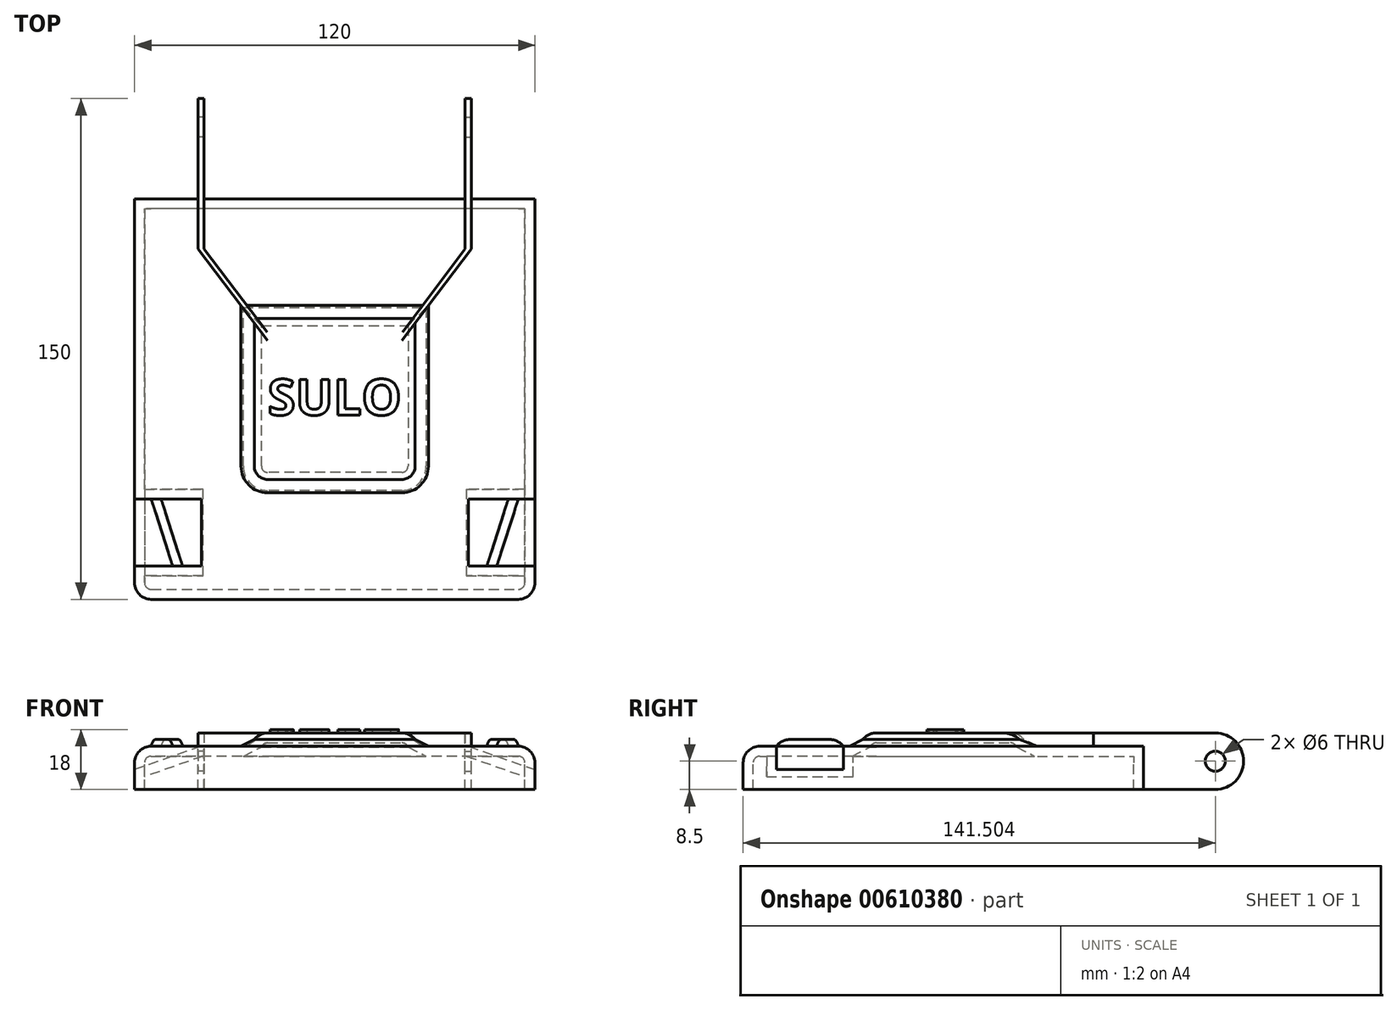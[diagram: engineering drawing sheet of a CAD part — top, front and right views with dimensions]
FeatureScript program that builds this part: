
annotation { "Feature Type Name" : "Feature", "Feature Type Description" : "" }
export const myFeature = defineFeature(function(context is Context, id is Id, definition is map)
    precondition{}
    {
        {
            var Q0;
            Q0=qCreatedBy(makeId("Top.planeOp"),FACE);
            var sketch = newSketch(context, id + "F0", { "sketchPlane" : qUnion([Q0])});
            skLineSegment(sketch, "E0.bottom", {"start": v(-158.38, 187.53) * mm, "end": v(-38.38, 187.53) * mm});
            skLineSegment(sketch, "E0.top", {"start": v(-158.38, 37.53) * mm, "end": v(-38.38, 37.53) * mm});
            skLineSegment(sketch, "E0.left", {"start": v(-158.38, 187.53) * mm, "end": v(-158.38, 37.53) * mm});
            skLineSegment(sketch, "E0.right", {"start": v(-38.38, 187.53) * mm, "end": v(-38.38, 37.53) * mm});
            skSolve(sketch);
        }
        {
            var Q0;
            Q0=makeQuery(id+"F0.imprint","IMPRINT",FACE,{"disambiguationData":[TD([[makeQuery(id+"F0.imprint","IMPRINT",EDGE,{"derivedFrom":sQuery(id+"F0.wireOp",EDGE,"E0.bottom")}),-1.0]])]});
            extrude(context, id + "F1", {"entities" : qUnion([Q0]), "depth" : 13 * mm, "offsetDistance" : 25 * mm});
        }
        {
            var Q0;
            Q0=makeQuery(id+"F1.opExtrude","CAP_FACE",FACE,{"disambiguationData":[OSD([sQuery(id+"F0.wireOp",EDGE,"E0.bottom"),sQuery(id+"F0.wireOp",EDGE,"E0.top"),sQuery(id+"F0.wireOp",EDGE,"E0.left"),sQuery(id+"F0.wireOp",EDGE,"E0.right")])],"isStart":false});
            var sketch = newSketch(context, id + "F2", { "sketchPlane" : qUnion([Q0])});
            skLineSegment(sketch, "E1", {"start": v(-73.38, 72.53) * mm, "end": v(-123.38, 72.53) * mm});
            skLineSegment(sketch, "E2", {"start": v(-123.38, 72.53) * mm, "end": v(-123.38, 121.53) * mm});
            skLineSegment(sketch, "E3", {"start": v(-122.38, 122.53) * mm, "end": v(-74.38, 122.53) * mm});
            skLineSegment(sketch, "E4", {"start": v(-73.38, 121.53) * mm, "end": v(-73.38, 72.53) * mm});
            skLineSegment(sketch, "E5", {"start": v(-139.38, 187.53) * mm, "end": v(-139.38, 142.53) * mm});
            skLineSegment(sketch, "E6", {"start": v(-139.38, 142.53) * mm, "end": v(-123.38, 121.53) * mm});
            skLineSegment(sketch, "E7", {"start": v(-122.38, 122.53) * mm, "end": v(-137.63, 142.53) * mm});
            skLineSegment(sketch, "E8", {"start": v(-137.63, 142.53) * mm, "end": v(-137.63, 187.53) * mm});
            skLineSegment(sketch, "E9", {"start": v(-57.38, 187.53) * mm, "end": v(-57.38, 142.53) * mm});
            skLineSegment(sketch, "E10", {"start": v(-57.38, 142.53) * mm, "end": v(-73.38, 121.53) * mm});
            skLineSegment(sketch, "E11", {"start": v(-59.38, 187.53) * mm, "end": v(-59.38, 142.53) * mm});
            skLineSegment(sketch, "E12", {"start": v(-59.38, 142.53) * mm, "end": v(-74.38, 122.53) * mm});
            skSolve(sketch);
        }
        {
            var Q0;
            Q0=makeQuery(id+"F2.imprint","IMPRINT",FACE,{"disambiguationData":[TD([[makeQuery(id+"F2.imprint","IMPRINT",EDGE,{"derivedFrom":sQuery(id+"F2.wireOp",EDGE,"E1")}),-1.0]])]});
            extrude(context, id + "F3", {"entities" : qUnion([Q0]), "operationType" : NewBodyOperationType.ADD, "depth" : 4 * mm, "offsetDistance" : 25 * mm});
        }
        {
            var Q0;
            {var subQ1=sQuery(id+"F0.wireOp",EDGE,"E0.left");var subQ3=sQuery(id+"F0.wireOp",EDGE,"E0.bottom");var subQ4=sQuery(id+"F0.wireOp",EDGE,"E0.right");var subQ5=sQuery(id+"F0.wireOp",EDGE,"E0.top");Q0=makeQuery(id+"F3.boolean.opBoolean","SPLIT",FACE,{"disambiguationData":[TD([makeQuery(id+"F1.opExtrude","SWEPT_FACE",FACE,{"disambiguationData":[OSD([subQ5])]})])],"derivedFrom":makeQuery(id+"F1.opExtrude","CAP_FACE",FACE,{"disambiguationData":[OSD([subQ3,subQ5,subQ1,subQ4])],"isStart":false})});}
            var sketch = newSketch(context, id + "F4", { "sketchPlane" : qUnion([Q0])});
            skLineSegment(sketch, "E13", {"start": v(-38.38, 187.53) * mm, "end": v(-38.38, 157.53) * mm});
            skLineSegment(sketch, "E14", {"start": v(-38.38, 157.53) * mm, "end": v(-57.38, 157.53) * mm});
            skLineSegment(sketch, "E15", {"start": v(-57.38, 157.53) * mm, "end": v(-57.38, 187.53) * mm});
            skLineSegment(sketch, "E16", {"start": v(-57.38, 187.53) * mm, "end": v(-38.38, 187.53) * mm});
            skLineSegment(sketch, "E17", {"start": v(-139.38, 187.53) * mm, "end": v(-139.38, 157.53) * mm});
            skLineSegment(sketch, "E18", {"start": v(-139.38, 157.53) * mm, "end": v(-158.38, 157.53) * mm});
            skLineSegment(sketch, "E19", {"start": v(-158.38, 157.53) * mm, "end": v(-158.38, 187.53) * mm});
            skLineSegment(sketch, "E20", {"start": v(-158.38, 187.53) * mm, "end": v(-139.38, 187.53) * mm});
            skSolve(sketch);
        }
        {
            var Q0;
            Q0 = qSketchRegion(id + "F4", true);
            extrude(context, id + "F5", {"entities" : qUnion([Q0]), "operationType" : NewBodyOperationType.REMOVE, "oppositeDirection" : true, "depth" : 25 * mm, "offsetDistance" : 25 * mm});
        }
        {
            var Q0;
            {var subQ1=sQuery(id+"F0.wireOp",EDGE,"E0.bottom");Q0=makeQuery(id+"F3.boolean.opBoolean","SPLIT",FACE,{"disambiguationData":[TD([makeQuery(id+"F3.opExtrude","SWEPT_FACE",FACE,{"disambiguationData":[OSD([sQuery(id+"F2.wireOp",EDGE,"E3")])]})])],"derivedFrom":makeQuery(id+"F1.opExtrude","CAP_FACE",FACE,{"disambiguationData":[OSD([subQ1,sQuery(id+"F0.wireOp",EDGE,"E0.top"),sQuery(id+"F0.wireOp",EDGE,"E0.left"),sQuery(id+"F0.wireOp",EDGE,"E0.right")])],"isStart":false})});}
            var sketch = newSketch(context, id + "F6", { "sketchPlane" : qUnion([Q0])});
            skLineSegment(sketch, "E21", {"start": v(-137.63, 187.53) * mm, "end": v(-59.38, 187.53) * mm});
            skLineSegment(sketch, "E22", {"start": v(-59.38, 187.53) * mm, "end": v(-59.38, 157.53) * mm});
            skLineSegment(sketch, "E23", {"start": v(-59.38, 157.53) * mm, "end": v(-137.63, 157.53) * mm});
            skLineSegment(sketch, "E24", {"start": v(-137.63, 157.53) * mm, "end": v(-137.63, 187.53) * mm});
            skSolve(sketch);
        }
        {
            var Q0;
            Q0 = qSketchRegion(id + "F6", true);
            extrude(context, id + "F7", {"entities" : qUnion([Q0]), "operationType" : NewBodyOperationType.REMOVE, "oppositeDirection" : true, "depth" : 25 * mm, "offsetDistance" : 25 * mm});
        }
        {
            var Q0;
            {var subQ0=sQuery(id+"F0.wireOp",EDGE,"E0.bottom");var subQ1=makeQuery(id+"F1.opExtrude","CAP_EDGE",EDGE,{"disambiguationData":[OSD([subQ0])],"isStart":false});Q0=makeQuery(id+"F3.opExtrude","CAP_EDGE",EDGE,{"disambiguationData":[OSD([subQ0]),TDD([makeQuery(id+"F2.imprint","IMPRINT",EDGE,{"disambiguationData":[TD([[makeQuery(id+"F2.imprint","INTERSECT",VERTEX,{"derivedFrom":[subQ1,sQuery(id+"F2.wireOp",EDGE,"E9")]}),1.0]])],"derivedFrom":subQ1})])],"isStart":false});}
            var Q1;
            {var subQ0=sQuery(id+"F2.wireOp",EDGE,"E9");var subQ1=sQuery(id+"F0.wireOp",EDGE,"E0.bottom");Q1=makeQuery(id+"F7.boolean.opBoolean","SPLIT",EDGE,{"disambiguationData":[TD([makeQuery(id+"F3.opExtrude","SWEPT_FACE",FACE,{"disambiguationData":[OSD([subQ0])]})])],"derivedFrom":makeQuery(id+"F1.opExtrude","CAP_EDGE",EDGE,{"disambiguationData":[OSD([subQ1])],"isStart":true})});}
            var Q2;
            {var subQ0=sQuery(id+"F0.wireOp",EDGE,"E0.bottom");var subQ1=makeQuery(id+"F1.opExtrude","CAP_EDGE",EDGE,{"disambiguationData":[OSD([subQ0])],"isStart":false});Q2=makeQuery(id+"F3.opExtrude","CAP_EDGE",EDGE,{"disambiguationData":[OSD([subQ0]),TDD([makeQuery(id+"F2.imprint","IMPRINT",EDGE,{"disambiguationData":[TD([[makeQuery(id+"F2.imprint","INTERSECT",VERTEX,{"derivedFrom":[subQ1,sQuery(id+"F2.wireOp",EDGE,"E5")]}),-1.0]])],"derivedFrom":subQ1})])],"isStart":false});}
            var Q3;
            {var subQ1=sQuery(id+"F2.wireOp",EDGE,"E5");var subQ2=sQuery(id+"F0.wireOp",EDGE,"E0.bottom");Q3=makeQuery(id+"F7.boolean.opBoolean","SPLIT",EDGE,{"disambiguationData":[TD([makeQuery(id+"F3.opExtrude","SWEPT_FACE",FACE,{"disambiguationData":[OSD([subQ1])]})])],"derivedFrom":makeQuery(id+"F1.opExtrude","CAP_EDGE",EDGE,{"disambiguationData":[OSD([subQ2])],"isStart":true})});}
            fillet(context, id + "F8", {"entities" : qUnion([Q0, Q1, Q2, Q3]), "radius" : 8.5 * mm, "tangentPropagation" : true, "allowEdgeOverflow" : false});
        }
        {
            var Q0;
            Q0=makeQuery(id+"F3.opExtrude","CAP_EDGE",EDGE,{"disambiguationData":[OSD([sQuery(id+"F2.wireOp",EDGE,"E4")])],"isStart":false});
            var Q1;
            Q1=makeQuery(id+"F3.opExtrude","CAP_EDGE",EDGE,{"disambiguationData":[OSD([sQuery(id+"F2.wireOp",EDGE,"E3")])],"isStart":false});
            var Q2;
            Q2=makeQuery(id+"F3.opExtrude","CAP_EDGE",EDGE,{"disambiguationData":[OSD([sQuery(id+"F2.wireOp",EDGE,"E1")])],"isStart":false});
            var Q3;
            Q3=makeQuery(id+"F3.opExtrude","CAP_EDGE",EDGE,{"disambiguationData":[OSD([sQuery(id+"F2.wireOp",EDGE,"E2")])],"isStart":false});
            fillet(context, id + "F9", {"entities" : qUnion([Q0, Q1, Q2, Q3]), "radius" : 5 * mm, "tangentPropagation" : true, "allowEdgeOverflow" : false});
        }
        {
            var Q0;
            Q0=makeQuery(id+"F9.opFillet","BLEND_EDGE",EDGE,{"blendedFrom":[makeQuery(id+"F3.opExtrude","CAP_EDGE",EDGE,{"disambiguationData":[OSD([sQuery(id+"F2.wireOp",EDGE,"E1")])],"isStart":false}),makeQuery(id+"F3.opExtrude","CAP_EDGE",EDGE,{"disambiguationData":[OSD([sQuery(id+"F2.wireOp",EDGE,"E2")])],"isStart":false})],"blendedInto":[]});
            var Q1;
            Q1=makeQuery(id+"F9.opFillet","BLEND_EDGE",EDGE,{"blendedFrom":[makeQuery(id+"F3.opExtrude","CAP_EDGE",EDGE,{"disambiguationData":[OSD([sQuery(id+"F2.wireOp",EDGE,"E1")])],"isStart":false}),makeQuery(id+"F3.opExtrude","CAP_EDGE",EDGE,{"disambiguationData":[OSD([sQuery(id+"F2.wireOp",EDGE,"E4")])],"isStart":false})],"blendedInto":[]});
            fillet(context, id + "F10", {"entities" : qUnion([Q0, Q1]), "radius" : 5 * mm, "tangentPropagation" : true, "allowEdgeOverflow" : false});
        }
        {
            var Q0;
            {var subQ1=sQuery(id+"F2.wireOp",EDGE,"E4");var subQ2=sQuery(id+"F0.wireOp",EDGE,"E0.left");var subQ4=sQuery(id+"F0.wireOp",EDGE,"E0.bottom");var subQ5=sQuery(id+"F0.wireOp",EDGE,"E0.right");var subQ6=sQuery(id+"F0.wireOp",EDGE,"E0.top");Q0=makeQuery(id+"F9.opFillet","BLEND_EDGE",EDGE,{"blendedFrom":[makeQuery(id+"F3.opExtrude","CAP_EDGE",EDGE,{"disambiguationData":[OSD([subQ1])],"isStart":false}),makeQuery(id+"F3.boolean.opBoolean","SPLIT",FACE,{"disambiguationData":[TD([makeQuery(id+"F1.opExtrude","SWEPT_FACE",FACE,{"disambiguationData":[OSD([subQ6])]})])],"derivedFrom":makeQuery(id+"F1.opExtrude","CAP_FACE",FACE,{"disambiguationData":[OSD([subQ4,subQ6,subQ2,subQ5])],"isStart":false})})],"blendedInto":[makeQuery(id+"F3.boolean.opBoolean","SPLIT",FACE,{"disambiguationData":[TD([makeQuery(id+"F1.opExtrude","SWEPT_FACE",FACE,{"disambiguationData":[OSD([subQ6])]})])],"derivedFrom":makeQuery(id+"F1.opExtrude","CAP_FACE",FACE,{"disambiguationData":[OSD([subQ4,subQ6,subQ2,subQ5])],"isStart":false})})]});}
            var Q1;
            {var subQ1=sQuery(id+"F2.wireOp",EDGE,"E3");var subQ2=sQuery(id+"F0.wireOp",EDGE,"E0.bottom");Q1=makeQuery(id+"F9.opFillet","BLEND_EDGE",EDGE,{"blendedFrom":[makeQuery(id+"F3.opExtrude","CAP_EDGE",EDGE,{"disambiguationData":[OSD([subQ1])],"isStart":false}),makeQuery(id+"F3.boolean.opBoolean","SPLIT",FACE,{"disambiguationData":[TD([makeQuery(id+"F3.opExtrude","SWEPT_FACE",FACE,{"disambiguationData":[OSD([subQ1])]})])],"derivedFrom":makeQuery(id+"F1.opExtrude","CAP_FACE",FACE,{"disambiguationData":[OSD([subQ2,sQuery(id+"F0.wireOp",EDGE,"E0.top"),sQuery(id+"F0.wireOp",EDGE,"E0.left"),sQuery(id+"F0.wireOp",EDGE,"E0.right")])],"isStart":false})})],"blendedInto":[makeQuery(id+"F3.boolean.opBoolean","SPLIT",FACE,{"disambiguationData":[TD([makeQuery(id+"F3.opExtrude","SWEPT_FACE",FACE,{"disambiguationData":[OSD([subQ1])]})])],"derivedFrom":makeQuery(id+"F1.opExtrude","CAP_FACE",FACE,{"disambiguationData":[OSD([subQ2,sQuery(id+"F0.wireOp",EDGE,"E0.top"),sQuery(id+"F0.wireOp",EDGE,"E0.left"),sQuery(id+"F0.wireOp",EDGE,"E0.right")])],"isStart":false})})]});}
            chamfer(context, id + "F11", {"entities" : qUnion([Q0, Q1]), "width" : 5 * mm, "tangentPropagation" : true});
        }
        {
            var Q0;
            Q0=makeQuery(id+"F5.boolean.opBoolean","MERGE",FACE,{"derivedFrom":[makeQuery(id+"F3.opExtrude","SWEPT_FACE",FACE,{"disambiguationData":[OSD([sQuery(id+"F2.wireOp",EDGE,"E9")])]}),makeQuery(id+"F5.opExtrude","SWEPT_FACE",FACE,{"disambiguationData":[OSD([sQuery(id+"F4.wireOp",EDGE,"E15")])]})]});
            var sketch = newSketch(context, id + "F12", { "sketchPlane" : qUnion([Q0])});
            skCircle(sketch, "E25", {"center": v(179.03, 8.5) * mm, "radius": 3 * mm});
            skSolve(sketch);
        }
        {
            var Q0;
            Q0=makeQuery(id+"F5.boolean.opBoolean","MERGE",FACE,{"derivedFrom":[makeQuery(id+"F3.opExtrude","SWEPT_FACE",FACE,{"disambiguationData":[OSD([sQuery(id+"F2.wireOp",EDGE,"E5")])]}),makeQuery(id+"F5.opExtrude","SWEPT_FACE",FACE,{"disambiguationData":[OSD([sQuery(id+"F4.wireOp",EDGE,"E17")])]})]});
            var sketch = newSketch(context, id + "F13", { "sketchPlane" : qUnion([Q0])});
            skCircle(sketch, "E26", {"center": v(-179.03, 8.5) * mm, "radius": 3 * mm});
            skSolve(sketch);
        }
        {
            var Q0;
            Q0 = qSketchRegion(id + "F13", true);
            extrude(context, id + "F14", {"entities" : qUnion([Q0]), "operationType" : NewBodyOperationType.REMOVE, "oppositeDirection" : true, "depth" : 25 * mm, "offsetDistance" : 25 * mm});
        }
        {
            var Q0;
            Q0=makeQuery(id+"F12.imprint","IMPRINT",FACE,{"disambiguationData":[TD([[makeQuery(id+"F12.imprint","IMPRINT",EDGE,{"derivedFrom":sQuery(id+"F12.wireOp",EDGE,"E25")}),1.0]])]});
            extrude(context, id + "F15", {"entities" : qUnion([Q0]), "operationType" : NewBodyOperationType.REMOVE, "oppositeDirection" : true, "depth" : 25 * mm, "offsetDistance" : 25 * mm});
        }
        {
            var Q0;
            {var subQ1=sQuery(id+"F0.wireOp",EDGE,"E0.left");var subQ3=sQuery(id+"F0.wireOp",EDGE,"E0.bottom");var subQ4=sQuery(id+"F0.wireOp",EDGE,"E0.right");var subQ5=sQuery(id+"F0.wireOp",EDGE,"E0.top");Q0=makeQuery(id+"F3.boolean.opBoolean","SPLIT",FACE,{"disambiguationData":[TD([makeQuery(id+"F1.opExtrude","SWEPT_FACE",FACE,{"disambiguationData":[OSD([subQ5])]})])],"derivedFrom":makeQuery(id+"F1.opExtrude","CAP_FACE",FACE,{"disambiguationData":[OSD([subQ3,subQ5,subQ1,subQ4])],"isStart":false})});}
            var sketch = newSketch(context, id + "F16", { "sketchPlane" : qUnion([Q0])});
            skLineSegment(sketch, "E27", {"start": v(-38.38, 47.53) * mm, "end": v(-58.38, 47.53) * mm});
            skLineSegment(sketch, "E28", {"start": v(-58.38, 47.53) * mm, "end": v(-58.38, 67.53) * mm});
            skLineSegment(sketch, "E29", {"start": v(-58.38, 67.53) * mm, "end": v(-38.38, 67.53) * mm});
            skLineSegment(sketch, "E30", {"start": v(-38.38, 67.53) * mm, "end": v(-38.38, 47.53) * mm});
            skSolve(sketch);
        }
        {
            var Q0;
            Q0=makeQuery(id+"F16.imprint","IMPRINT",FACE,{"disambiguationData":[TD([[makeQuery(id+"F16.imprint","IMPRINT",EDGE,{"derivedFrom":sQuery(id+"F16.wireOp",EDGE,"E27")}),-1.0]])]});
            extrude(context, id + "F17", {"entities" : qUnion([Q0]), "operationType" : NewBodyOperationType.REMOVE, "oppositeDirection" : true, "depth" : 7 * mm, "offsetDistance" : 25 * mm});
        }
        {
            var Q0;
            Q0=makeQuery(id+"F17.boolean.opBoolean","COPY",EDGE,{"derivedFrom":makeQuery(id+"F17.opExtrude","CAP_EDGE",EDGE,{"disambiguationData":[OSD([sQuery(id+"F16.wireOp",EDGE,"E28")])],"isStart":false})});
            chamfer(context, id + "F18", {"entities" : qUnion([Q0]), "chamferType" : ChamferType.TWO_OFFSETS, "width1" : 7 * mm, "oppositeDirection" : false, "width2" : 20 * mm, "tangentPropagation" : true});
        }
        {
            var Q0;
            {var subQ1=sQuery(id+"F0.wireOp",EDGE,"E0.left");var subQ3=sQuery(id+"F0.wireOp",EDGE,"E0.bottom");var subQ4=sQuery(id+"F0.wireOp",EDGE,"E0.right");var subQ5=sQuery(id+"F0.wireOp",EDGE,"E0.top");Q0=makeQuery(id+"F3.boolean.opBoolean","SPLIT",FACE,{"disambiguationData":[TD([makeQuery(id+"F1.opExtrude","SWEPT_FACE",FACE,{"disambiguationData":[OSD([subQ5])]})])],"derivedFrom":makeQuery(id+"F1.opExtrude","CAP_FACE",FACE,{"disambiguationData":[OSD([subQ3,subQ5,subQ1,subQ4])],"isStart":false})});}
            var sketch = newSketch(context, id + "F19", { "sketchPlane" : qUnion([Q0])});
            skLineSegment(sketch, "E31", {"start": v(-158.38, 47.53) * mm, "end": v(-138.38, 47.53) * mm});
            skLineSegment(sketch, "E32", {"start": v(-138.38, 47.53) * mm, "end": v(-138.38, 67.53) * mm});
            skLineSegment(sketch, "E33", {"start": v(-138.38, 67.53) * mm, "end": v(-158.38, 67.53) * mm});
            skLineSegment(sketch, "E34", {"start": v(-158.38, 67.53) * mm, "end": v(-158.38, 47.53) * mm});
            skSolve(sketch);
        }
        {
            var Q0;
            Q0=makeQuery(id+"F19.imprint","IMPRINT",FACE,{"disambiguationData":[TD([[makeQuery(id+"F19.imprint","IMPRINT",EDGE,{"derivedFrom":sQuery(id+"F19.wireOp",EDGE,"E31")}),1.0]])]});
            extrude(context, id + "F20", {"entities" : qUnion([Q0]), "operationType" : NewBodyOperationType.REMOVE, "oppositeDirection" : true, "depth" : 7 * mm, "offsetDistance" : 25 * mm});
        }
        {
            var Q0;
            Q0=makeQuery(id+"F20.boolean.opBoolean","COPY",EDGE,{"derivedFrom":makeQuery(id+"F20.opExtrude","CAP_EDGE",EDGE,{"disambiguationData":[OSD([sQuery(id+"F19.wireOp",EDGE,"E32")])],"isStart":false})});
            chamfer(context, id + "F21", {"entities" : qUnion([Q0]), "chamferType" : ChamferType.TWO_OFFSETS, "width1" : 20 * mm, "oppositeDirection" : false, "width2" : 7 * mm, "tangentPropagation" : true});
        }
        {
            var Q0;
            {var subQ1=sQuery(id+"F0.wireOp",EDGE,"E0.left");var subQ3=sQuery(id+"F0.wireOp",EDGE,"E0.bottom");var subQ4=sQuery(id+"F0.wireOp",EDGE,"E0.right");var subQ5=sQuery(id+"F0.wireOp",EDGE,"E0.top");Q0=makeQuery(id+"F3.boolean.opBoolean","SPLIT",FACE,{"disambiguationData":[TD([makeQuery(id+"F1.opExtrude","SWEPT_FACE",FACE,{"disambiguationData":[OSD([subQ5])]})])],"derivedFrom":makeQuery(id+"F1.opExtrude","CAP_FACE",FACE,{"disambiguationData":[OSD([subQ3,subQ5,subQ1,subQ4])],"isStart":false})});}
            var sketch = newSketch(context, id + "F22", { "sketchPlane" : qUnion([Q0])});
            skLineSegment(sketch, "E35", {"start": v(-153.38, 67.53) * mm, "end": v(-146.98, 47.53) * mm});
            skLineSegment(sketch, "E36", {"start": v(-146.98, 47.53) * mm, "end": v(-143.98, 47.53) * mm});
            skLineSegment(sketch, "E37", {"start": v(-143.98, 47.53) * mm, "end": v(-150.38, 67.53) * mm});
            skLineSegment(sketch, "E38", {"start": v(-150.38, 67.53) * mm, "end": v(-153.38, 67.53) * mm});
            skSolve(sketch);
        }
        {
            var Q0;
            Q0 = qSketchRegion(id + "F22", true);
            extrude(context, id + "F23", {"entities" : qUnion([Q0]), "depth" : 2 * mm, "offsetDistance" : 25 * mm});
        }
        {
            var Q0;
            Q0=makeQuery(id+"F23.opExtrude","CAP_EDGE",EDGE,{"disambiguationData":[OSD([sQuery(id+"F22.wireOp",EDGE,"E38")])],"isStart":false});
            var Q1;
            Q1=makeQuery(id+"F23.opExtrude","CAP_EDGE",EDGE,{"disambiguationData":[OSD([sQuery(id+"F22.wireOp",EDGE,"E36")])],"isStart":false});
            fillet(context, id + "F24", {"entities" : qUnion([Q0, Q1]), "radius" : 5 * mm, "tangentPropagation" : true, "allowEdgeOverflow" : false});
        }
        {
            var Q0;
            {var subQ1=sQuery(id+"F0.wireOp",EDGE,"E0.left");var subQ3=sQuery(id+"F0.wireOp",EDGE,"E0.bottom");var subQ4=sQuery(id+"F0.wireOp",EDGE,"E0.right");var subQ5=sQuery(id+"F0.wireOp",EDGE,"E0.top");Q0=makeQuery(id+"F3.boolean.opBoolean","SPLIT",FACE,{"disambiguationData":[TD([makeQuery(id+"F1.opExtrude","SWEPT_FACE",FACE,{"disambiguationData":[OSD([subQ5])]})])],"derivedFrom":makeQuery(id+"F1.opExtrude","CAP_FACE",FACE,{"disambiguationData":[OSD([subQ3,subQ5,subQ1,subQ4])],"isStart":false})});}
            var sketch = newSketch(context, id + "F25", { "sketchPlane" : qUnion([Q0])});
            skLineSegment(sketch, "E39", {"start": v(-43.38, 67.53) * mm, "end": v(-49.79, 47.53) * mm});
            skLineSegment(sketch, "E40", {"start": v(-49.79, 47.53) * mm, "end": v(-52.79, 47.53) * mm});
            skLineSegment(sketch, "E41", {"start": v(-52.79, 47.53) * mm, "end": v(-46.38, 67.53) * mm});
            skLineSegment(sketch, "E42", {"start": v(-46.38, 67.53) * mm, "end": v(-43.38, 67.53) * mm});
            skSolve(sketch);
        }
        {
            var Q0;
            Q0=makeQuery(id+"F25.imprint","IMPRINT",FACE,{"disambiguationData":[TD([[makeQuery(id+"F25.imprint","IMPRINT",EDGE,{"derivedFrom":sQuery(id+"F25.wireOp",EDGE,"E39")}),-1.0]])]});
            extrude(context, id + "F26", {"entities" : qUnion([Q0]), "depth" : 2 * mm, "offsetDistance" : 25 * mm});
        }
        {
            var Q0;
            Q0=makeQuery(id+"F26.opExtrude","CAP_EDGE",EDGE,{"disambiguationData":[OSD([sQuery(id+"F25.wireOp",EDGE,"E40")])],"isStart":false});
            var Q1;
            Q1=makeQuery(id+"F26.opExtrude","CAP_EDGE",EDGE,{"disambiguationData":[OSD([sQuery(id+"F25.wireOp",EDGE,"E42")])],"isStart":false});
            fillet(context, id + "F27", {"entities" : qUnion([Q0, Q1]), "radius" : 5 * mm, "tangentPropagation" : true, "allowEdgeOverflow" : false});
        }
        {
            var Q0;
            {var subQ0=sQuery(id+"F0.wireOp",EDGE,"E0.left");Q0=makeQuery(id+"F20.boolean.opBoolean","SPLIT",EDGE,{"disambiguationData":[TD([makeQuery(id+"F5.boolean.opBoolean","COPY",FACE,{"derivedFrom":makeQuery(id+"F5.opExtrude","SWEPT_FACE",FACE,{"disambiguationData":[OSD([sQuery(id+"F4.wireOp",EDGE,"E18")])]})})])],"derivedFrom":makeQuery(id+"F1.opExtrude","CAP_EDGE",EDGE,{"disambiguationData":[OSD([subQ0])],"isStart":false})});}
            var Q1;
            Q1=makeQuery(id+"F5.boolean.opBoolean","COPY",EDGE,{"derivedFrom":makeQuery(id+"F5.opExtrude","CAP_EDGE",EDGE,{"disambiguationData":[OSD([sQuery(id+"F4.wireOp",EDGE,"E18")])],"isStart":true})});
            var Q2;
            Q2=makeQuery(id+"F7.boolean.opBoolean","COPY",EDGE,{"derivedFrom":makeQuery(id+"F7.opExtrude","CAP_EDGE",EDGE,{"disambiguationData":[OSD([sQuery(id+"F6.wireOp",EDGE,"E23")])],"isStart":true})});
            var Q3;
            Q3=makeQuery(id+"F5.boolean.opBoolean","COPY",EDGE,{"derivedFrom":makeQuery(id+"F5.opExtrude","CAP_EDGE",EDGE,{"disambiguationData":[OSD([sQuery(id+"F4.wireOp",EDGE,"E14")])],"isStart":true})});
            var Q4;
            {var subQ0=sQuery(id+"F0.wireOp",EDGE,"E0.right");Q4=makeQuery(id+"F17.boolean.opBoolean","SPLIT",EDGE,{"disambiguationData":[TD([makeQuery(id+"F5.boolean.opBoolean","COPY",FACE,{"derivedFrom":makeQuery(id+"F5.opExtrude","SWEPT_FACE",FACE,{"disambiguationData":[OSD([sQuery(id+"F4.wireOp",EDGE,"E14")])]})})])],"derivedFrom":makeQuery(id+"F1.opExtrude","CAP_EDGE",EDGE,{"disambiguationData":[OSD([subQ0])],"isStart":false})});}
            var Q5;
            {var subQ0=sQuery(id+"F0.wireOp",EDGE,"E0.right");var subQ1=sQuery(id+"F0.wireOp",EDGE,"E0.top");Q5=makeQuery(id+"F17.boolean.opBoolean","SPLIT",EDGE,{"disambiguationData":[TD([makeQuery(id+"F1.opExtrude","SWEPT_FACE",FACE,{"disambiguationData":[OSD([subQ1])]})])],"derivedFrom":makeQuery(id+"F1.opExtrude","CAP_EDGE",EDGE,{"disambiguationData":[OSD([subQ0])],"isStart":false})});}
            var Q6;
            Q6=makeQuery(id+"F1.opExtrude","CAP_EDGE",EDGE,{"disambiguationData":[OSD([sQuery(id+"F0.wireOp",EDGE,"E0.top")])],"isStart":false});
            var Q7;
            {var subQ0=sQuery(id+"F0.wireOp",EDGE,"E0.left");var subQ1=sQuery(id+"F0.wireOp",EDGE,"E0.top");Q7=makeQuery(id+"F20.boolean.opBoolean","SPLIT",EDGE,{"disambiguationData":[TD([makeQuery(id+"F1.opExtrude","SWEPT_FACE",FACE,{"disambiguationData":[OSD([subQ1])]})])],"derivedFrom":makeQuery(id+"F1.opExtrude","CAP_EDGE",EDGE,{"disambiguationData":[OSD([subQ0])],"isStart":false})});}
            fillet(context, id + "F28", {"entities" : qUnion([Q0, Q1, Q2, Q3, Q4, Q5, Q6, Q7]), "radius" : 5 * mm, "tangentPropagation" : true, "allowEdgeOverflow" : false});
        }
        {
            var Q0;
            {var subQ0=sQuery(id+"F0.wireOp",EDGE,"E0.left");var subQ1=sQuery(id+"F0.wireOp",EDGE,"E0.top");Q0=makeQuery(id+"F28.opFillet","BLEND_EDGE",EDGE,{"blendedFrom":[makeQuery(id+"F1.opExtrude","CAP_EDGE",EDGE,{"disambiguationData":[OSD([subQ1])],"isStart":false}),makeQuery(id+"F20.boolean.opBoolean","SPLIT",EDGE,{"disambiguationData":[TD([makeQuery(id+"F1.opExtrude","SWEPT_FACE",FACE,{"disambiguationData":[OSD([subQ1])]})])],"derivedFrom":makeQuery(id+"F1.opExtrude","CAP_EDGE",EDGE,{"disambiguationData":[OSD([subQ0])],"isStart":false})})],"blendedInto":[]});}
            var Q1;
            {var subQ0=sQuery(id+"F0.wireOp",EDGE,"E0.right");var subQ1=sQuery(id+"F0.wireOp",EDGE,"E0.top");Q1=makeQuery(id+"F28.opFillet","BLEND_EDGE",EDGE,{"blendedFrom":[makeQuery(id+"F1.opExtrude","CAP_EDGE",EDGE,{"disambiguationData":[OSD([subQ1])],"isStart":false}),makeQuery(id+"F17.boolean.opBoolean","SPLIT",EDGE,{"disambiguationData":[TD([makeQuery(id+"F1.opExtrude","SWEPT_FACE",FACE,{"disambiguationData":[OSD([subQ1])]})])],"derivedFrom":makeQuery(id+"F1.opExtrude","CAP_EDGE",EDGE,{"disambiguationData":[OSD([subQ0])],"isStart":false})})],"blendedInto":[]});}
            var Q2;
            {var subQ0=sQuery(id+"F0.wireOp",EDGE,"E0.left");var subQ1=sQuery(id+"F4.wireOp",EDGE,"E18");Q2=makeQuery(id+"F28.opFillet","BLEND_EDGE",EDGE,{"blendedFrom":[makeQuery(id+"F5.boolean.opBoolean","COPY",EDGE,{"derivedFrom":makeQuery(id+"F5.opExtrude","CAP_EDGE",EDGE,{"disambiguationData":[OSD([subQ1])],"isStart":true})}),makeQuery(id+"F20.boolean.opBoolean","SPLIT",EDGE,{"disambiguationData":[TD([makeQuery(id+"F5.boolean.opBoolean","COPY",FACE,{"derivedFrom":makeQuery(id+"F5.opExtrude","SWEPT_FACE",FACE,{"disambiguationData":[OSD([subQ1])]})})])],"derivedFrom":makeQuery(id+"F1.opExtrude","CAP_EDGE",EDGE,{"disambiguationData":[OSD([subQ0])],"isStart":false})})],"blendedInto":[]});}
            var Q3;
            {var subQ0=sQuery(id+"F0.wireOp",EDGE,"E0.right");var subQ1=sQuery(id+"F4.wireOp",EDGE,"E14");Q3=makeQuery(id+"F28.opFillet","BLEND_EDGE",EDGE,{"blendedFrom":[makeQuery(id+"F5.boolean.opBoolean","COPY",EDGE,{"derivedFrom":makeQuery(id+"F5.opExtrude","CAP_EDGE",EDGE,{"disambiguationData":[OSD([subQ1])],"isStart":true})}),makeQuery(id+"F17.boolean.opBoolean","SPLIT",EDGE,{"disambiguationData":[TD([makeQuery(id+"F5.boolean.opBoolean","COPY",FACE,{"derivedFrom":makeQuery(id+"F5.opExtrude","SWEPT_FACE",FACE,{"disambiguationData":[OSD([subQ1])]})})])],"derivedFrom":makeQuery(id+"F1.opExtrude","CAP_EDGE",EDGE,{"disambiguationData":[OSD([subQ0])],"isStart":false})})],"blendedInto":[]});}
            fillet(context, id + "F29", {"entities" : qUnion([Q0, Q1, Q2, Q3]), "radius" : 5 * mm, "tangentPropagation" : true, "allowEdgeOverflow" : false});
        }
        {
            var Q0;
            Q0=makeQuery(id+"F1.opExtrude","CAP_FACE",FACE,{"disambiguationData":[OSD([sQuery(id+"F0.wireOp",EDGE,"E0.bottom"),sQuery(id+"F0.wireOp",EDGE,"E0.top"),sQuery(id+"F0.wireOp",EDGE,"E0.left"),sQuery(id+"F0.wireOp",EDGE,"E0.right")])],"isStart":true});
            shell(context, id + "F30", {"entities" : qUnion([Q0]), "thickness" : 3 * mm});
        }
        {
            var Q0;
            Q0=makeQuery(id+"F3.opExtrude","CAP_FACE",FACE,{"disambiguationData":[OSD([sQuery(id+"F0.wireOp",EDGE,"E0.bottom"),sQuery(id+"F2.wireOp",EDGE,"E1"),sQuery(id+"F2.wireOp",EDGE,"E2"),sQuery(id+"F2.wireOp",EDGE,"E3"),sQuery(id+"F2.wireOp",EDGE,"E4"),sQuery(id+"F2.wireOp",EDGE,"E5"),sQuery(id+"F2.wireOp",EDGE,"E6"),sQuery(id+"F2.wireOp",EDGE,"E7"),sQuery(id+"F2.wireOp",EDGE,"E8"),sQuery(id+"F2.wireOp",EDGE,"E9"),sQuery(id+"F2.wireOp",EDGE,"E10"),sQuery(id+"F2.wireOp",EDGE,"E11"),sQuery(id+"F2.wireOp",EDGE,"E12")])],"isStart":false});
            var sketch = newSketch(context, id + "F31", { "sketchPlane" : qUnion([Q0])});
            skText(sketch, "E43", { "text": "SULO", "fontName": "OpenSans-Bold.ttf"});
            const initialGuessF31  = {"E43": [-0.11848, 0.09272, 1, 0, 0.01082]};
            skSetInitialGuess(sketch, initialGuessF31);
            skSolve(sketch);
        }
        {
            var Q0;
            Q0 = qSketchRegion(id + "F31", true);
            var Q1;
            Q1 = qConstructionFilter(qBodyType(qCreatedBy(id + "F31" ,EDGE), BodyType.WIRE), ConstructionObject.NO);
            extrude(context, id + "F32", {"entities" : qUnion([Q0]), "operationType" : NewBodyOperationType.ADD, "surfaceEntities" : qUnion([Q1]), "depth" : 1 * mm, "offsetDistance" : 25 * mm});
        }
    });
